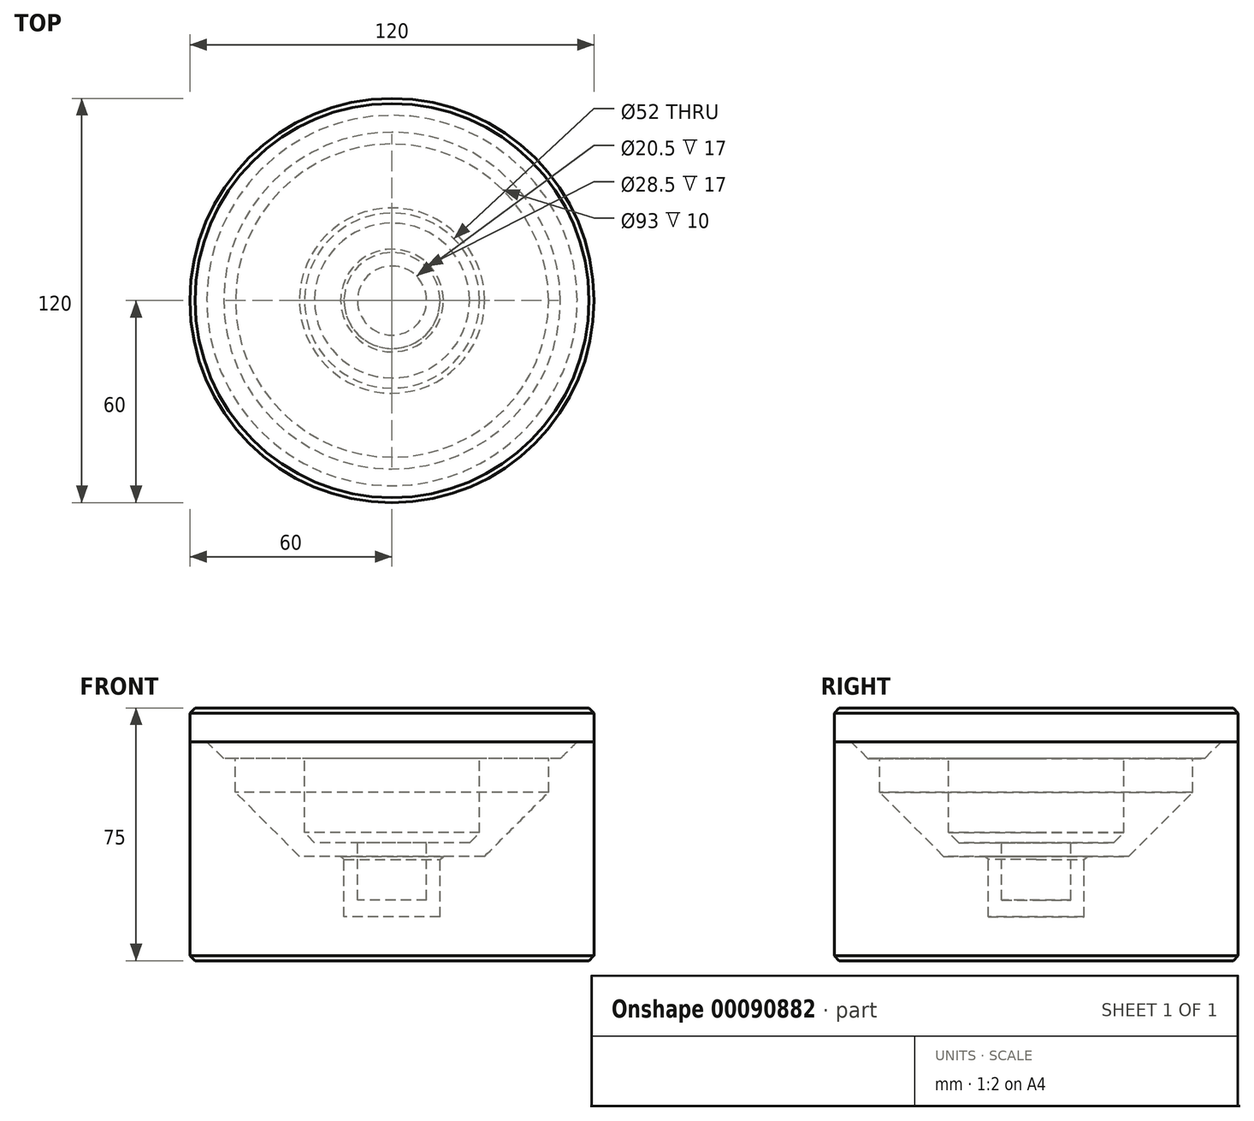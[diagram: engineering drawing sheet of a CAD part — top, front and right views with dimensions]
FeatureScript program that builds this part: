
annotation { "Feature Type Name" : "Feature", "Feature Type Description" : "" }
export const myFeature = defineFeature(function(context is Context, id is Id, definition is map)
    precondition{}
    {
        {
            var Q0;
            Q0=qCreatedBy(makeId("Front.planeOp"),FACE);
            var sketch = newSketch(context, id + "F0", { "sketchPlane" : qUnion([Q0])});
            skLineSegment(sketch, "E0.bottom", {"start": v(60, 30) * mm, "end": v(-60, 30) * mm});
            skLineSegment(sketch, "E0.top", {"start": v(60, -30) * mm, "end": v(-60, -30) * mm});
            skLineSegment(sketch, "E0.left", {"start": v(60, 30) * mm, "end": v(60, -30) * mm});
            skLineSegment(sketch, "E0.right", {"start": v(-60, 30) * mm, "end": v(-60, -30) * mm});
            skPoint(sketch, "E0.middle", {"position": v(0, 0) * mm});
            skLineSegment(sketch, "E1", {"start": v(0, 121.28) * mm, "end": v(0, -93.9) * mm});
            skLineSegment(sketch, "E2.top", {"start": v(10.25, -12) * mm, "end": v(-10.25, -12) * mm});
            skLineSegment(sketch, "E3", {"start": v(-60, 20) * mm, "end": v(60, 20) * mm});
            skLineSegment(sketch, "E4", {"start": v(-46.5, 30) * mm, "end": v(-46.5, 20) * mm});
            skLineSegment(sketch, "E5", {"start": v(46.5, 30) * mm, "end": v(46.5, 20) * mm});
            skLineSegment(sketch, "E6.left", {"start": v(23, 9) * mm, "end": v(23, 5) * mm});
            skLineSegment(sketch, "E6.right", {"start": v(-26, 8) * mm, "end": v(-26, 5) * mm});
            skLineSegment(sketch, "E7", {"start": v(-26, 8) * mm, "end": v(-26, 30) * mm});
            skLineSegment(sketch, "E8", {"start": v(23, 5) * mm, "end": v(23, 30) * mm});
            skLineSegment(sketch, "E9", {"start": v(-60, 30) * mm, "end": v(-60, 45) * mm});
            skLineSegment(sketch, "E10", {"start": v(-60, 45) * mm, "end": v(60, 45) * mm});
            skLineSegment(sketch, "E11", {"start": v(60, 45) * mm, "end": v(60, 30) * mm});
            skPoint(sketch, "E12.orphan", {"position": v(0, 65.26) * mm});
            skLineSegment(sketch, "E13", {"start": v(-46.5, 20) * mm, "end": v(-27.5, 1) * mm});
            skPoint(sketch, "E14.end.orphan", {"position": v(-36.38, 30) * mm});
            skPoint(sketch, "E15.end.orphan", {"position": v(-60, 76) * mm});
            skPoint(sketch, "E16.MirrorCS.end.orphan", {"position": v(36.38, 30) * mm});
            skPoint(sketch, "E17.MirrorCS.end.orphan", {"position": v(60, 76) * mm});
            skLineSegment(sketch, "E18", {"start": v(-23, 5) * mm, "end": v(-10.25, 5) * mm});
            skLineSegment(sketch, "E19", {"start": v(-10.25, 5) * mm, "end": v(-10.25, -12) * mm});
            skLineSegment(sketch, "E20.MirrorCS", {"start": v(23, 5) * mm, "end": v(10.25, 5) * mm});
            skLineSegment(sketch, "E21.MirrorCS", {"start": v(10.25, 5) * mm, "end": v(10.25, -12) * mm});
            skPoint(sketch, "E22.orphan", {"position": v(-40, 5) * mm});
            skPoint(sketch, "E23.orphan", {"position": v(20, 30) * mm});
            skLineSegment(sketch, "E24", {"start": v(-27.5, 1) * mm, "end": v(-14.25, 1) * mm});
            skLineSegment(sketch, "E25", {"start": v(-14.25, 1) * mm, "end": v(-14.25, -17) * mm});
            skLineSegment(sketch, "E26", {"start": v(-14.25, -17) * mm, "end": v(0, -17) * mm});
            skLineSegment(sketch, "E27", {"start": v(-26, 8) * mm, "end": v(-23, 5) * mm});
            skLineSegment(sketch, "E28.MirrorCS", {"start": v(26, 8) * mm, "end": v(23, 5) * mm});
            skLineSegment(sketch, "E29.MirrorCS", {"start": v(14.25, 1) * mm, "end": v(14.25, -17) * mm});
            skLineSegment(sketch, "E30.MirrorCS", {"start": v(14.25, -17) * mm, "end": v(0, -17) * mm});
            skLineSegment(sketch, "E31.MirrorCS", {"start": v(46.5, 20) * mm, "end": v(27.5, 1) * mm});
            skLineSegment(sketch, "E32.MirrorCS", {"start": v(27.5, 1) * mm, "end": v(14.25, 1) * mm});
            skLineSegment(sketch, "E33", {"start": v(-60, 35) * mm, "end": v(-55, 35) * mm});
            skLineSegment(sketch, "E34", {"start": v(-55, 35) * mm, "end": v(-50, 30) * mm});
            skLineSegment(sketch, "E35", {"start": v(26, 8) * mm, "end": v(26, 30) * mm});
            skSolve(sketch);
        }
        {
            var Q0;
            {var subQ3=sQuery(id+"F0.wireOp",EDGE,"E4");Q0=makeQuery(id+"F0.imprint","IMPRINT",FACE,{"disambiguationData":[TD([[makeQuery(id+"F0.imprint","IMPRINT",EDGE,{"derivedFrom":subQ3}),-1.0]])]});}
            var Q1;
            {var subQ4=sQuery(id+"F0.wireOp",EDGE,"E13");Q1=makeQuery(id+"F0.imprint","IMPRINT",FACE,{"disambiguationData":[TD([[makeQuery(id+"F0.imprint","IMPRINT",EDGE,{"derivedFrom":subQ4}),-1.0]])]});}
            var Q2;
            {var subQ4=sQuery(id+"F0.wireOp",EDGE,"E33");Q2=makeQuery(id+"F0.imprint","IMPRINT",FACE,{"disambiguationData":[TD([[makeQuery(id+"F0.imprint","IMPRINT",EDGE,{"derivedFrom":subQ4}),-1.0]])]});}
            var Q3;
            Q3=sQuery(id+"F0.wireOp",EDGE,"E1");
            revolve(context, id + "F1", {"entities" : qUnion([Q0, Q1, Q2]), "axis" : qUnion([Q3]), "revolveType" : RevolveType.FULL});
        }
        {
            var Q0;
            {var subQ0=sQuery(id+"F0.wireOp",EDGE,"E7");var subQ1=sQuery(id+"F0.wireOp",EDGE,"E0.bottom");var subQ2=makeQuery(id+"F0.imprint","INTERSECT",VERTEX,{"derivedFrom":[subQ1,subQ0]});Q0=makeQuery(id+"F0.imprint","IMPRINT",FACE,{"disambiguationData":[TD([[makeQuery(id+"F0.imprint","IMPRINT",EDGE,{"disambiguationData":[TD([[subQ2,1.0]])],"derivedFrom":subQ1}),1.0]])]});}
            var Q1;
            Q1=makeQuery(id+"F0.imprint","IMPRINT",FACE,{"disambiguationData":[TD([[makeQuery(id+"F0.imprint","IMPRINT",EDGE,{"derivedFrom":sQuery(id+"F0.wireOp",EDGE,"E18")}),1.0]])]});
            var Q2;
            {var subQ10=sQuery(id+"F0.wireOp",EDGE,"E33");Q2=makeQuery(id+"F0.imprint","IMPRINT",FACE,{"disambiguationData":[TD([[makeQuery(id+"F0.imprint","IMPRINT",EDGE,{"derivedFrom":subQ10}),1.0]])]});}
            var Q3;
            Q3=sQuery(id+"F0.wireOp",EDGE,"E1");
            revolve(context, id + "F2", {"entities" : qUnion([Q0, Q1, Q2]), "axis" : qUnion([Q3]), "revolveType" : RevolveType.FULL});
        }
        {
            var Q0;
            {var subQ0=sQuery(id+"F0.wireOp",EDGE,"E4");Q0=makeQuery(id+"F0.imprint","IMPRINT",FACE,{"disambiguationData":[TD([[makeQuery(id+"F0.imprint","IMPRINT",EDGE,{"derivedFrom":subQ0}),1.0]])]});}
            var Q1;
            {var subQ2=sQuery(id+"F0.wireOp",EDGE,"E13");Q1=makeQuery(id+"F0.imprint","IMPRINT",FACE,{"disambiguationData":[TD([[makeQuery(id+"F0.imprint","IMPRINT",EDGE,{"derivedFrom":subQ2}),1.0]])]});}
            var Q2;
            Q2=sQuery(id+"F0.wireOp",EDGE,"E1");
            revolve(context, id + "F3", {"entities" : qUnion([Q0, Q1]), "axis" : qUnion([Q2]), "revolveType" : RevolveType.FULL});
        }
        {
            var Q0;
            Q0=makeQuery(id+"F2.opRevolve","SWEPT_EDGE",EDGE,{"disambiguationData":[OSD([sQuery(id+"F0.wireOp",EDGE,"E9"),sQuery(id+"F0.wireOp",EDGE,"E10")])]});
            chamfer(context, id + "F4", {"entities" : qUnion([Q0]), "width" : 1.5 * mm, "tangentPropagation" : true});
        }
        {
            var Q0;
            Q0=makeQuery(id+"F1.opRevolve","SWEPT_EDGE",EDGE,{"disambiguationData":[OSD([sQuery(id+"F0.wireOp",EDGE,"E0.top"),sQuery(id+"F0.wireOp",EDGE,"E0.right")])]});
            chamfer(context, id + "F5", {"entities" : qUnion([Q0]), "width" : 1.5 * mm, "tangentPropagation" : true});
        }
        {
            var Q0;
            Q0=makeQuery(id+"F1.opRevolve","SWEPT_EDGE",EDGE,{"disambiguationData":[OSD([sQuery(id+"F0.wireOp",EDGE,"E24"),sQuery(id+"F0.wireOp",EDGE,"E25")])]});
            chamfer(context, id + "F6", {"entities" : qUnion([Q0]), "width" : 1 * mm, "tangentPropagation" : true});
        }
    });
